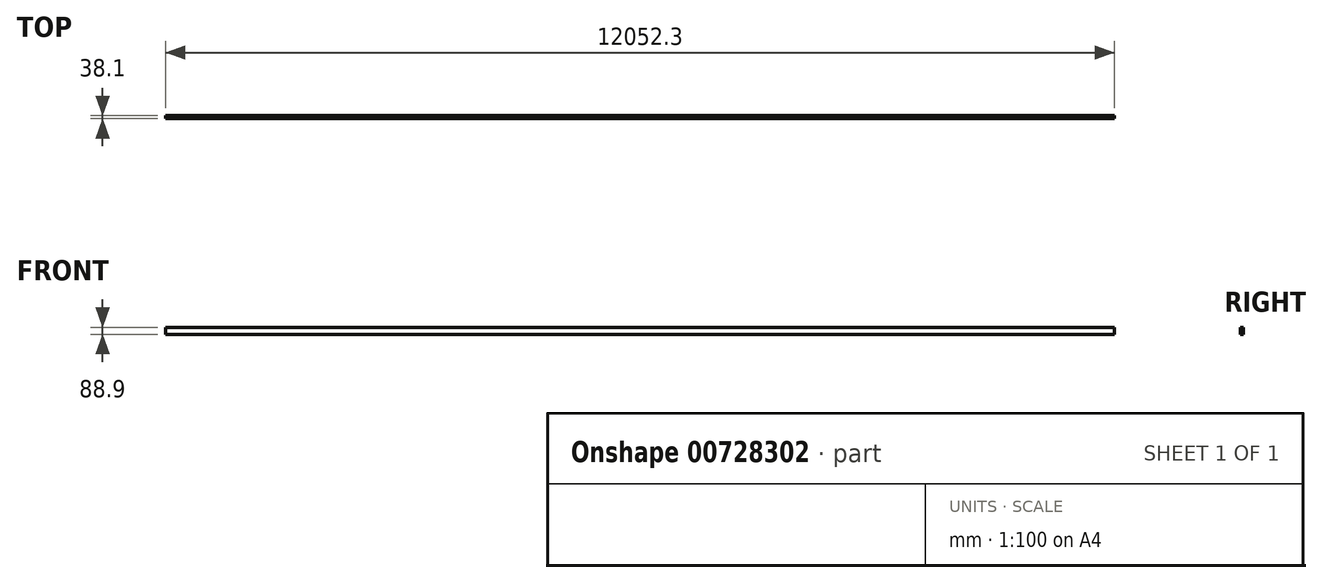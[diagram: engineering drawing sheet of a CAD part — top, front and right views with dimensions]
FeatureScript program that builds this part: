
annotation { "Feature Type Name" : "Feature", "Feature Type Description" : "" }
export const myFeature = defineFeature(function(context is Context, id is Id, definition is map)
    precondition{}
    {
        {
            var Q0;
            Q0=qCreatedBy(makeId("Front.planeOp"),FACE);
            var sketch = newSketch(context, id + "F0", { "sketchPlane" : qUnion([Q0])});
            skPoint(sketch, "E0.middle", {"position": v(0, 0) * mm});
            skLineSegment(sketch, "E1.bottom", {"start": v(-6026.15, -44.45) * mm, "end": v(6026.15, -44.45) * mm});
            skLineSegment(sketch, "E1.top", {"start": v(-6026.15, 44.45) * mm, "end": v(6026.15, 44.45) * mm});
            skLineSegment(sketch, "E1.left", {"start": v(-6026.15, -44.45) * mm, "end": v(-6026.15, 44.45) * mm});
            skLineSegment(sketch, "E1.right", {"start": v(6026.15, -44.45) * mm, "end": v(6026.15, 44.45) * mm});
            skSolve(sketch);
        }
        {
            var Q0;
            Q0=qSketchRegion(id+"F0",true);
            extrude(context, id + "F1", {"entities" : qUnion([Q0]), "depth" : 38.1 * mm, "offsetDistance" : 25.4 * mm});
        }
    });
